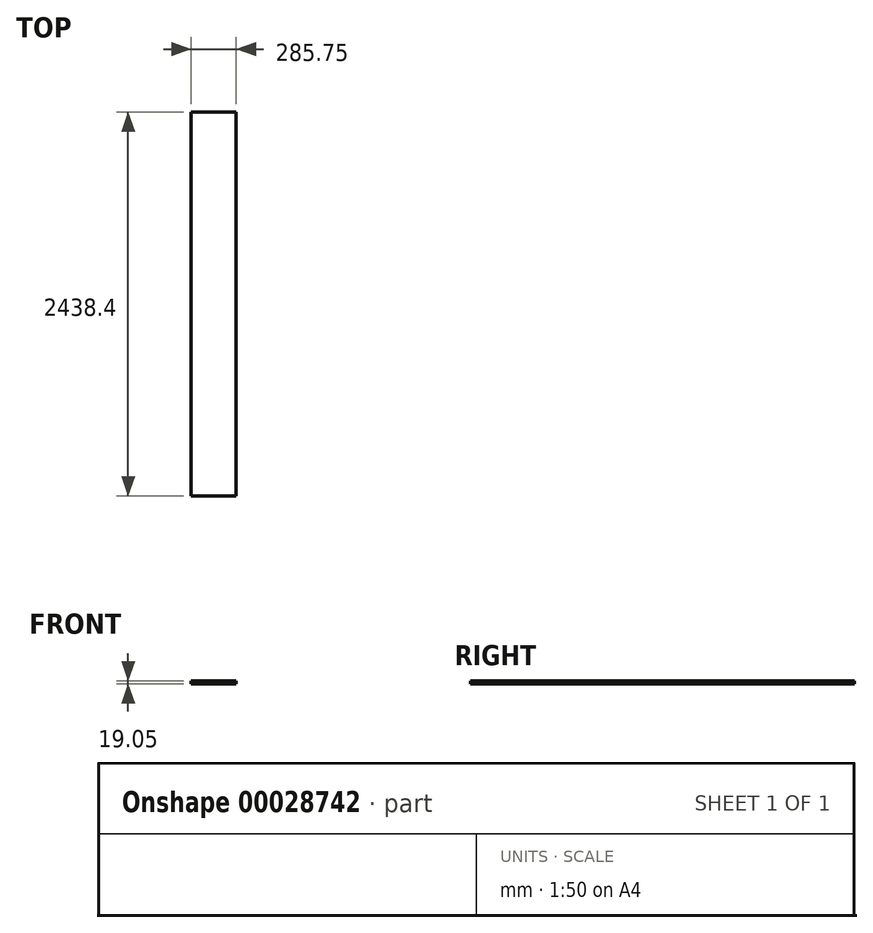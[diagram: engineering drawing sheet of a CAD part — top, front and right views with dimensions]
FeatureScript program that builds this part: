
annotation { "Feature Type Name" : "Feature", "Feature Type Description" : "" }
export const myFeature = defineFeature(function(context is Context, id is Id, definition is map)
    precondition{}
    {
        {
            var Q0;
            Q0=qCreatedBy(makeId("Top.planeOp"),FACE);
            var sketch = newSketch(context, id + "F0", { "sketchPlane" : qUnion([Q0])});
            skLineSegment(sketch, "E0.bottom", {"start": v(-55.94, 2418.1) * mm, "end": v(229.81, 2418.1) * mm});
            skLineSegment(sketch, "E0.top", {"start": v(-55.94, -20.3) * mm, "end": v(229.81, -20.3) * mm});
            skLineSegment(sketch, "E0.left", {"start": v(-55.94, 2418.1) * mm, "end": v(-55.94, -20.3) * mm});
            skLineSegment(sketch, "E0.right", {"start": v(229.81, 2418.1) * mm, "end": v(229.81, -20.3) * mm});
            skSolve(sketch);
        }
        {
            var Q0;
            Q0 = qSketchRegion(id + "F0", true);
            extrude(context, id + "F1", {"entities" : qUnion([Q0]), "depth" : 19.05 * mm});
        }
    });
